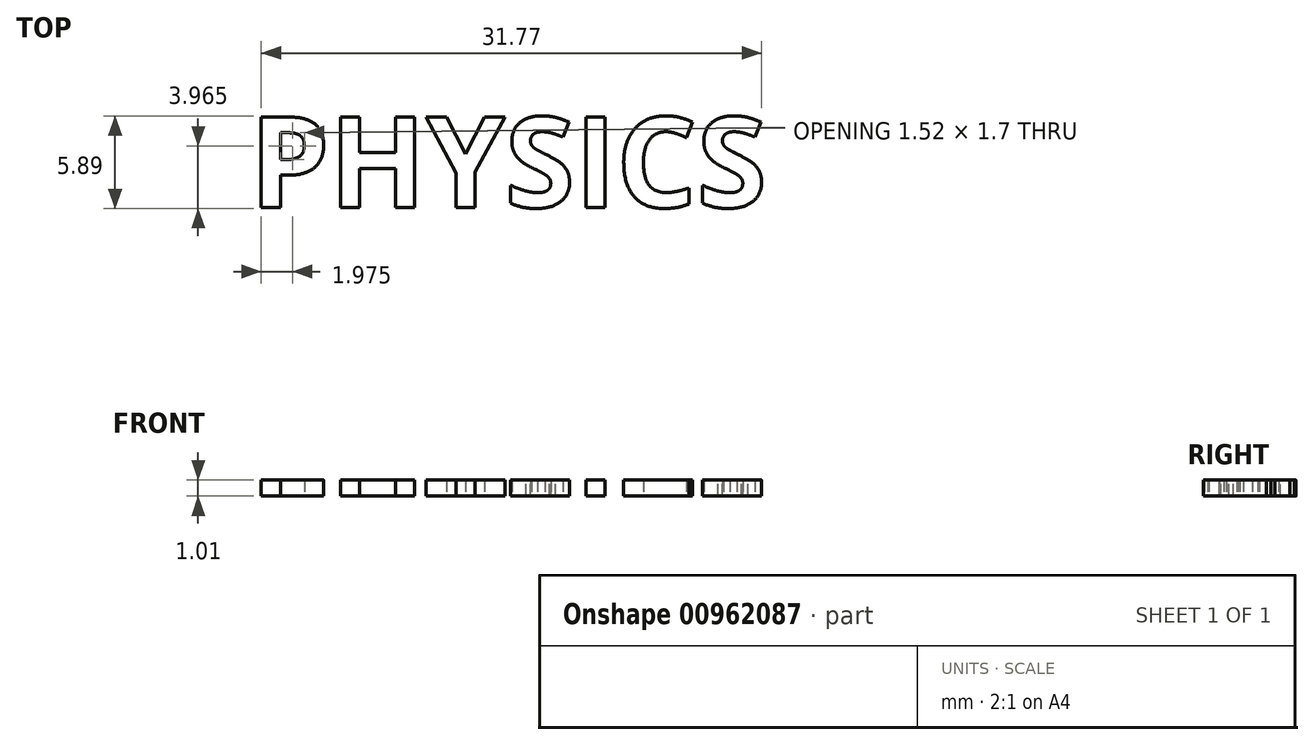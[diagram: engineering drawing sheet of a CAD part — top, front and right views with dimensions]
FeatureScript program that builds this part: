
annotation { "Feature Type Name" : "Feature", "Feature Type Description" : "" }
export const myFeature = defineFeature(function(context is Context, id is Id, definition is map)
    precondition{}
    {
        {
            var Q0;
            Q0=qCreatedBy(makeId("Top.planeOp"),FACE);
            var sketch = newSketch(context, id + "F0", { "sketchPlane" : qUnion([Q0])});
            skLineSegment(sketch, "E0.bottom", {"start": v(17.5, -3.75) * mm, "end": v(-17.5, -3.75) * mm});
            skLineSegment(sketch, "E0.top", {"start": v(17.5, 3.75) * mm, "end": v(-17.5, 3.75) * mm});
            skLineSegment(sketch, "E0.left", {"start": v(17.5, -3.75) * mm, "end": v(17.5, 3.75) * mm});
            skLineSegment(sketch, "E0.right", {"start": v(-17.5, -3.75) * mm, "end": v(-17.5, 3.75) * mm});
            skPoint(sketch, "E0.middle", {"position": v(0, 0) * mm});
            skSolve(sketch);
        }
        {
            var Q0;
            Q0=makeQuery(id+"F0.imprint","IMPRINT",FACE,{"disambiguationData":[TD([[makeQuery(id+"F0.imprint","IMPRINT",EDGE,{"derivedFrom":sQuery(id+"F0.wireOp",EDGE,"E0.bottom")}),-1.0]])]});
            extrude(context, id + "F1", {"entities" : qUnion([Q0]), "depth" : 0.4 * mm, "offsetDistance" : 25 * mm});
        }
        {
            var Q0;
            Q0=makeQuery(id+"F1.opExtrude","CAP_FACE",FACE,{"disambiguationData":[OSD([sQuery(id+"F0.wireOp",EDGE,"E0.bottom"),sQuery(id+"F0.wireOp",EDGE,"E0.top"),sQuery(id+"F0.wireOp",EDGE,"E0.left"),sQuery(id+"F0.wireOp",EDGE,"E0.right")])],"isStart":false});
            var sketch = newSketch(context, id + "F2", { "sketchPlane" : qUnion([Q0])});
            skText(sketch, "E1", { "text": "PHYSICS", "fontName": "OpenSans-Bold.ttf"});
            skPoint(sketch, "E2", {"position": v(-17.5, 0) * mm});
            const initialGuessF2  = {"E1": [-0.0175, -0.00289, 1, 0, 0.00578]};
            skSetInitialGuess(sketch, initialGuessF2);
            skSolve(sketch);
        }
        {
            var Q0;
            Q0=qSketchRegion(id+"F2",true);
            extrude(context, id + "F3", {"entities" : qUnion([Q0]), "operationType" : NewBodyOperationType.ADD, "depth" : 1 * mm, "offsetDistance" : 25 * mm});
        }
        {
            var Q0;
            Q0=makeQuery(id+"F1.opExtrude","SWEPT_FACE",FACE,{"disambiguationData":[OSD([sQuery(id+"F0.wireOp",EDGE,"E0.bottom")])]});
            var sketch = newSketch(context, id + "F4", { "sketchPlane" : qUnion([Q0])});
            skLineSegment(sketch, "E3.bottom", {"start": v(-17.5, 0) * mm, "end": v(17.5, 0) * mm});
            skLineSegment(sketch, "E3.top", {"start": v(-17.5, 0.39) * mm, "end": v(17.5, 0.39) * mm});
            skLineSegment(sketch, "E3.left", {"start": v(-17.5, 0) * mm, "end": v(-17.5, 0.39) * mm});
            skLineSegment(sketch, "E3.right", {"start": v(17.5, 0) * mm, "end": v(17.5, 0.39) * mm});
            skSolve(sketch);
        }
        {
            var Q0;
            Q0 = qSketchRegion(id + "F4", true);
            extrude(context, id + "F5", {"entities" : qUnion([Q0]), "operationType" : NewBodyOperationType.REMOVE, "endBound" : BoundingType.THROUGH_ALL, "oppositeDirection" : true, "depth" : 25 * mm, "offsetDistance" : 25 * mm});
        }
    });
